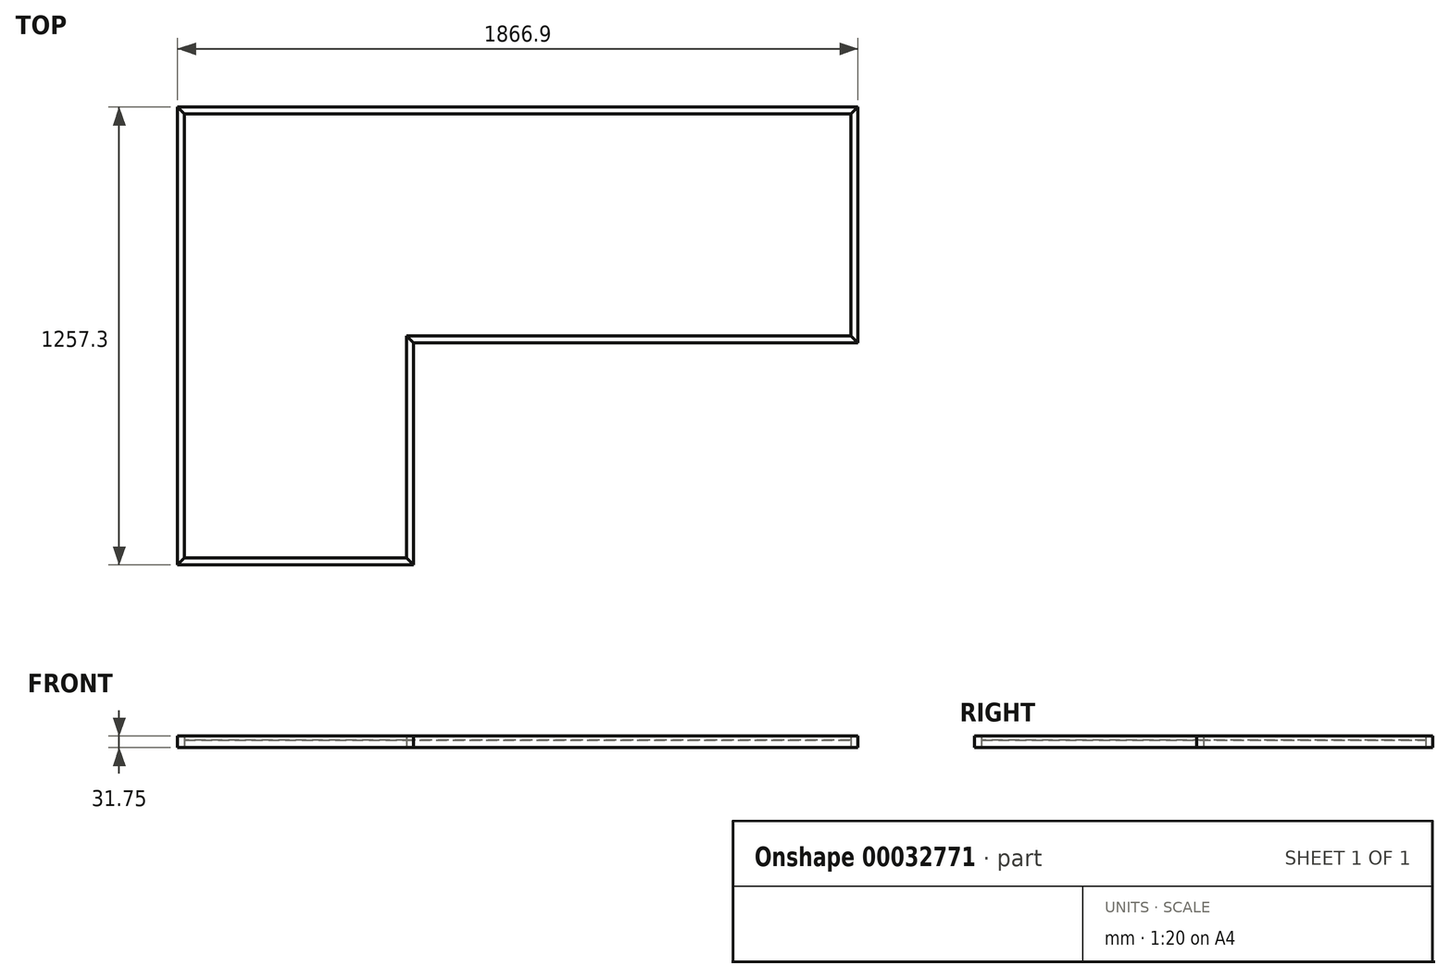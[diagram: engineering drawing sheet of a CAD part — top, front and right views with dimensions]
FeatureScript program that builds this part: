
annotation { "Feature Type Name" : "Feature", "Feature Type Description" : "" }
export const myFeature = defineFeature(function(context is Context, id is Id, definition is map)
    precondition{}
    {
        {
            var Q0;
            Q0=qCreatedBy(makeId("Top.planeOp"),FACE);
            var sketch = newSketch(context, id + "F0", { "sketchPlane" : qUnion([Q0])});
            skLineSegment(sketch, "E0", {"start": v(-609.6, -609.6) * mm, "end": v(-609.6, 609.6) * mm});
            skLineSegment(sketch, "E1", {"start": v(-609.6, 609.6) * mm, "end": v(1219.2, 609.6) * mm});
            skLineSegment(sketch, "E2", {"start": v(1219.2, 609.6) * mm, "end": v(1219.2, 0) * mm});
            skLineSegment(sketch, "E3", {"start": v(1219.2, 0) * mm, "end": v(0, 0) * mm});
            skLineSegment(sketch, "E4", {"start": v(0, 0) * mm, "end": v(0, -609.6) * mm});
            skLineSegment(sketch, "E5", {"start": v(0, -609.6) * mm, "end": v(-609.6, -609.6) * mm});
            skLineSegment(sketch, "E6", {"start": v(-628.65, 628.65) * mm, "end": v(-628.65, -628.65) * mm});
            skLineSegment(sketch, "E7", {"start": v(-628.65, -628.65) * mm, "end": v(19.05, -628.65) * mm});
            skLineSegment(sketch, "E8", {"start": v(19.05, -628.65) * mm, "end": v(19.05, -19.05) * mm});
            skLineSegment(sketch, "E9", {"start": v(19.05, -19.05) * mm, "end": v(1238.25, -19.05) * mm});
            skLineSegment(sketch, "E10", {"start": v(1238.25, -19.05) * mm, "end": v(1238.25, 628.65) * mm});
            skLineSegment(sketch, "E11", {"start": v(1238.25, 628.65) * mm, "end": v(-628.65, 628.65) * mm});
            skLineSegment(sketch, "E12", {"start": v(19.05, -628.65) * mm, "end": v(0, -609.6) * mm});
            skLineSegment(sketch, "E13", {"start": v(19.05, -19.05) * mm, "end": v(0, 0) * mm});
            skLineSegment(sketch, "E14", {"start": v(1238.25, -19.05) * mm, "end": v(1219.2, 0) * mm});
            skLineSegment(sketch, "E15", {"start": v(1219.2, 609.6) * mm, "end": v(1238.25, 628.65) * mm});
            skLineSegment(sketch, "E16", {"start": v(-609.6, 609.6) * mm, "end": v(-628.65, 628.65) * mm});
            skLineSegment(sketch, "E17", {"start": v(-628.65, -628.65) * mm, "end": v(-609.6, -609.6) * mm});
            skSolve(sketch);
        }
        {
            var Q0;
            Q0=makeQuery(id+"F0.imprint","IMPRINT",FACE,{"disambiguationData":[TD([[makeQuery(id+"F0.imprint","IMPRINT",EDGE,{"derivedFrom":sQuery(id+"F0.wireOp",EDGE,"E0")}),-1.0]])]});
            extrude(context, id + "F1", {"entities" : qUnion([Q0]), "depth" : 21.43 * mm});
        }
        {
            var Q0;
            Q0=makeQuery(id+"F0.imprint","IMPRINT",FACE,{"disambiguationData":[TD([[makeQuery(id+"F0.imprint","IMPRINT",EDGE,{"derivedFrom":sQuery(id+"F0.wireOp",EDGE,"E0")}),1.0]])]});
            extrude(context, id + "F2", {"entities" : qUnion([Q0]), "depth" : 31.75 * mm});
        }
        {
            var Q0;
            Q0=makeQuery(id+"F0.imprint","IMPRINT",FACE,{"disambiguationData":[TD([[makeQuery(id+"F0.imprint","IMPRINT",EDGE,{"derivedFrom":sQuery(id+"F0.wireOp",EDGE,"E5")}),1.0]])]});
            extrude(context, id + "F3", {"entities" : qUnion([Q0]), "depth" : 31.75 * mm});
        }
        {
            var Q0;
            Q0=makeQuery(id+"F0.imprint","IMPRINT",FACE,{"disambiguationData":[TD([[makeQuery(id+"F0.imprint","IMPRINT",EDGE,{"derivedFrom":sQuery(id+"F0.wireOp",EDGE,"E4")}),1.0]])]});
            extrude(context, id + "F4", {"entities" : qUnion([Q0]), "depth" : 31.75 * mm});
        }
        {
            var Q0;
            Q0=makeQuery(id+"F0.imprint","IMPRINT",FACE,{"disambiguationData":[TD([[makeQuery(id+"F0.imprint","IMPRINT",EDGE,{"derivedFrom":sQuery(id+"F0.wireOp",EDGE,"E3")}),1.0]])]});
            extrude(context, id + "F5", {"entities" : qUnion([Q0]), "depth" : 31.75 * mm});
        }
        {
            var Q0;
            Q0=makeQuery(id+"F0.imprint","IMPRINT",FACE,{"disambiguationData":[TD([[makeQuery(id+"F0.imprint","IMPRINT",EDGE,{"derivedFrom":sQuery(id+"F0.wireOp",EDGE,"E2")}),1.0]])]});
            extrude(context, id + "F6", {"entities" : qUnion([Q0]), "depth" : 31.75 * mm});
        }
        {
            var Q0;
            Q0=makeQuery(id+"F0.imprint","IMPRINT",FACE,{"disambiguationData":[TD([[makeQuery(id+"F0.imprint","IMPRINT",EDGE,{"derivedFrom":sQuery(id+"F0.wireOp",EDGE,"E1")}),1.0]])]});
            extrude(context, id + "F7", {"entities" : qUnion([Q0]), "depth" : 31.75 * mm});
        }
    });
